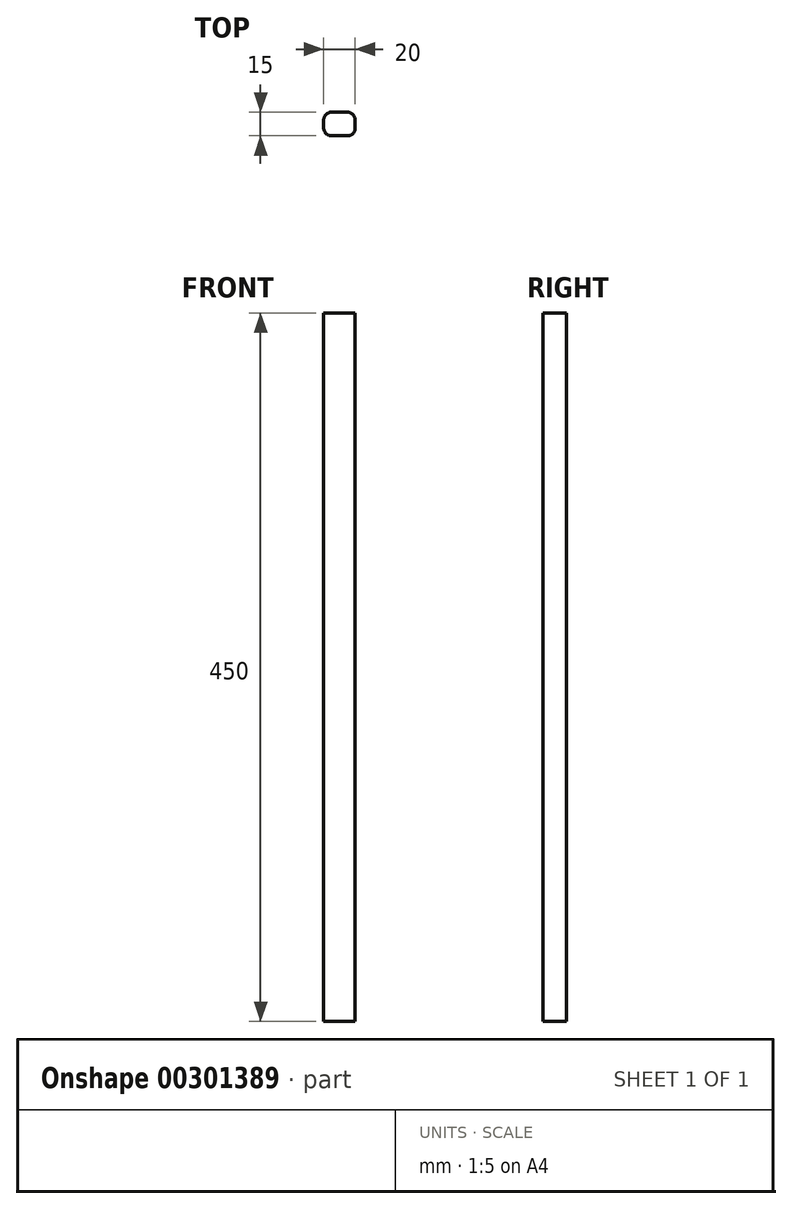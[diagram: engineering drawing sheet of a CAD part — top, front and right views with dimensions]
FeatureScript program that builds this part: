
annotation { "Feature Type Name" : "Feature", "Feature Type Description" : "" }
export const myFeature = defineFeature(function(context is Context, id is Id, definition is map)
    precondition{}
    {
        {
            var Q0;
            Q0=qCreatedBy(makeId("Top.planeOp"),FACE);
            var sketch = newSketch(context, id + "F0", { "sketchPlane" : qUnion([Q0])});
            skLineSegment(sketch, "E0.bottom", {"start": v(0, 0) * mm, "end": v(20, 0) * mm});
            skLineSegment(sketch, "E0.top", {"start": v(0, -15) * mm, "end": v(20, -15) * mm});
            skLineSegment(sketch, "E0.left", {"start": v(0, 0) * mm, "end": v(0, -15) * mm});
            skLineSegment(sketch, "E0.right", {"start": v(20, 0) * mm, "end": v(20, -15) * mm});
            skSolve(sketch);
        }
        {
            var Q0;
            Q0=makeQuery(id+"F0.imprint","IMPRINT",FACE,{"disambiguationData":[TD([[makeQuery(id+"F0.imprint","IMPRINT",EDGE,{"derivedFrom":sQuery(id+"F0.wireOp",EDGE,"E0.bottom")}),-1.0]])]});
            extrude(context, id + "F1", {"entities" : qUnion([Q0]), "depth" : 450 * mm});
        }
        {
            var Q0;
            Q0=makeQuery(id+"F1.opExtrude","SWEPT_EDGE",EDGE,{"disambiguationData":[OSD([sQuery(id+"F0.wireOp",EDGE,"E0.top"),sQuery(id+"F0.wireOp",EDGE,"E0.right")])]});
            var Q1;
            Q1=makeQuery(id+"F1.opExtrude","SWEPT_EDGE",EDGE,{"disambiguationData":[OSD([sQuery(id+"F0.wireOp",EDGE,"E0.bottom"),sQuery(id+"F0.wireOp",EDGE,"E0.right")])]});
            var Q2;
            Q2=makeQuery(id+"F1.opExtrude","SWEPT_EDGE",EDGE,{"disambiguationData":[OSD([sQuery(id+"F0.wireOp",EDGE,"E0.bottom"),sQuery(id+"F0.wireOp",EDGE,"E0.left")])]});
            var Q3;
            Q3=makeQuery(id+"F1.opExtrude","SWEPT_EDGE",EDGE,{"disambiguationData":[OSD([sQuery(id+"F0.wireOp",EDGE,"E0.top"),sQuery(id+"F0.wireOp",EDGE,"E0.left")])]});
            fillet(context, id + "F2", {"entities" : qUnion([Q0, Q1, Q2, Q3]), "radius" : 5 * mm, "tangentPropagation" : true, "allowEdgeOverflow" : false});
        }
    });
